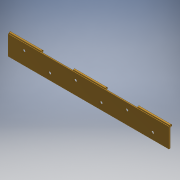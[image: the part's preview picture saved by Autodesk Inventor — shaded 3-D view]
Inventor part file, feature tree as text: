
AUTODESK INVENTOR PART (.ipt)
format: ipt  version: 2018 (Build 220112000, 112)  size: 164,864 bytes
history: native  units: mm
features: extrude x5, sketch x5, plane x1, hole x1
ambient origin geometry x8: Origin, YZ Plane, XZ Plane, XY Plane, X Axis, Y Axis, Z Axis, Center Point
bodies: Solid1 (feature_tree)
feature tree (12):
  extrude  "Extrusion1"  Depth=30.0mm
  sketch  "Sketch2"  dims[d2=2.0mm d3=0.0mm d4=2.5mm]
  extrude  "Extrusion2"  Depth=2.0mm
  extrude  "Extrusion3"  Depth=3.0mm
  sketch  "Sketch3"  dims[d5=3.0mm d6=3.5mm]
  plane  "Work Plane1"
  hole  "Hole1"  [1 undecoded]
  extrude  "Extrusion6"  Depth=10.0mm
  extrude  "Extrusion7"  Depth=10.0mm
  sketch  "Sketch1"  dims[d0=250.0mm d1=30.0mm]
  sketch  "Sketch5"  dims[d7=250.0mm d8=0.0mm d9=250.0mm d10=0.0mm]
  sketch  "Sketch6"  dims[d23=40.0mm d24=5.0mm d25=40.0mm d26=40.0mm d27=40.0mm d28=40.0mm d29=10.0mm d30=10.0mm d31=4.0mm d32=6.0mm d33=8.0mm d34=2.0mm d35=90.0deg d36=8.0mm d37=20.594885mm d38=50.0mm d39=2.75mm d40=50.0mm d41=2.75mm d42=50.0mm d43=50.0mm d44=250.0mm d45=0.0mm d46=10.0mm d47=0.0mm]
note: 1 required parameter value undecoded (feature->parameter linkage not recoverable at this tier; creation-order binding heuristic only, values carry confidence <= 0.55)
